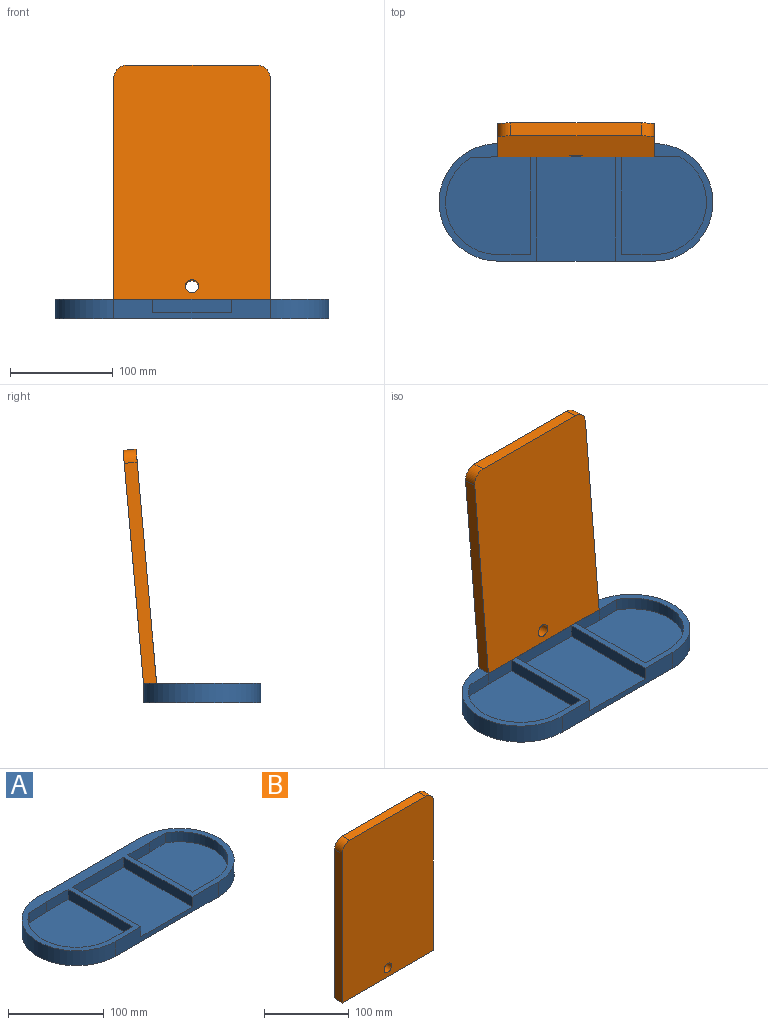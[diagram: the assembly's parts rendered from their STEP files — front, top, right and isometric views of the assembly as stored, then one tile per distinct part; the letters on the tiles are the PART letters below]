
ASSEMBLY  parts=2 mates=1
PART A: 22 faces, bbox 266.7x114.3x19.1 mm
  f0: plane 152.4x19.05mm, normal (0,-1,0), area 1938.9mm2, adj f1,f2,f4,f5,f6,f8,f9
  f1: plane 266.7x114.3mm, normal (0,0,1), area 6003.9mm2, adj f0,f2,f3,f4,f6,f7,f8,f10
  f2: cylinder r=57.15mm len=114.3mm, axis (0,0,1), area 3420.3mm2, adj f0,f1,f3,f5
  f3: plane 152.4x19.05mm, normal (0,1,0), area 2903.2mm2, adj f1,f2,f4,f5
  f4: cylinder r=57.15mm len=114.3mm, axis (0,0,1), area 3420.3mm2, adj f0,f1,f3,f5
  f5: plane 266.7x114.3mm, normal (0,0,-1), area 27680.1mm2, adj f0,f2,f3,f4
  f6: plane 101.6x12.7mm, normal (-1,0,0), area 1290.3mm2, adj f0,f1,f7,f9
  f7: plane 75.93x12.7mm, normal (0,-1,0), area 964.4mm2, adj f1,f6,f8,f9
  f8: plane 101.6x12.7mm, normal (1,0,0), area 1290.3mm2, adj f0,f1,f7,f9
  f9: plane 101.6x75.93mm, normal (0,0,1), area 7714.8mm2, adj f0,f6,f7,f8
  f10: plane 95.25x12.7mm, normal (-1,0,0), area 1209.7mm2, adj f1,f11,f14,f15
  f11: plane 31.88x12.7mm, normal (0,-1,0), area 404.9mm2, adj f1,f10,f12,f15
  f12: plane 26.5x12.7mm, normal (0.04,-1,0), area 336.9mm2, adj f1,f11,f13,f15
  f13: cylinder r=50.8mm len=94.14mm, axis (0,0,1), area 1672.7mm2, adj f1,f12,f14,f15
  f14: plane 31.88x12.7mm, normal (0,1,0), area 404.9mm2, adj f1,f10,f13,f15
  f15: plane 95.25x82.68mm, normal (0,0,1), area 6971.4mm2, adj f10,f11,f12,f13,f14
  f16: plane 23.84x12.7mm, normal (0.02,-1,0), area 302.8mm2, adj f1,f17,f20,f21
  f17: plane 31.88x12.7mm, normal (0,-1,0), area 404.9mm2, adj f1,f16,f18,f21
  f18: plane 95.25x12.7mm, normal (1,0,0), area 1209.7mm2, adj f1,f17,f19,f21
  f19: plane 31.88x12.7mm, normal (0,1,0), area 404.9mm2, adj f1,f18,f20,f21
  f20: cylinder r=50.8mm len=95.66mm, axis (0,0,1), area 1711.7mm2, adj f1,f16,f19,f21
  f21: plane 95.66x82.68mm, normal (0,0,1), area 6990.1mm2, adj f16,f17,f18,f19,f20
PART B: 9 faces, bbox 152.4x12.7x228.6 mm
  f0: plane 215.9x12.7mm, normal (-1,0,0), area 2734.9mm2, adj f4,f6,f7,f8
  f1: plane 215.9x12.7mm, normal (1,0,0), area 2734.9mm2, adj f2,f6,f7,f8
  f2: cylinder r=12.7mm len=12.7mm, axis (0,1,0), area 253.4mm2, adj f1,f3,f6,f7
  f3: plane 127x12.7mm, normal (0,0,1), area 1612.9mm2, adj f2,f4,f6,f7
  f4: cylinder r=12.7mm len=12.7mm, axis (0,1,0), area 253.4mm2, adj f0,f3,f6,f7
  f5: cylinder r=6.35mm len=12.7mm, axis (0,1,0), area 506.7mm2, adj f6,f7
  f6: plane 228.6x152.4mm, normal (0,-1,0), area 34642.7mm2, adj f0,f1,f2,f3,f4,f5,f8
  f7: plane 227.49x152.4mm, normal (0,1,0), area 34473.4mm2, adj f0,f1,f2,f3,f4,f5,f8
  f8: plane 152.4x12.7mm, normal (0,0.09,-1), area 1942.9mm2, adj f0,f1,f6,f7
PLACE A t=(-0.06,57.55,123.83)mm fixed
PLACE B rot(axis=(-1,0,0),5deg) t=(-0.06,67.41,122.28)mm
MATE fastened B.f8 <-> A.f1  axis (0,0,-1) through (-0.06,57.55,9.53)mm
